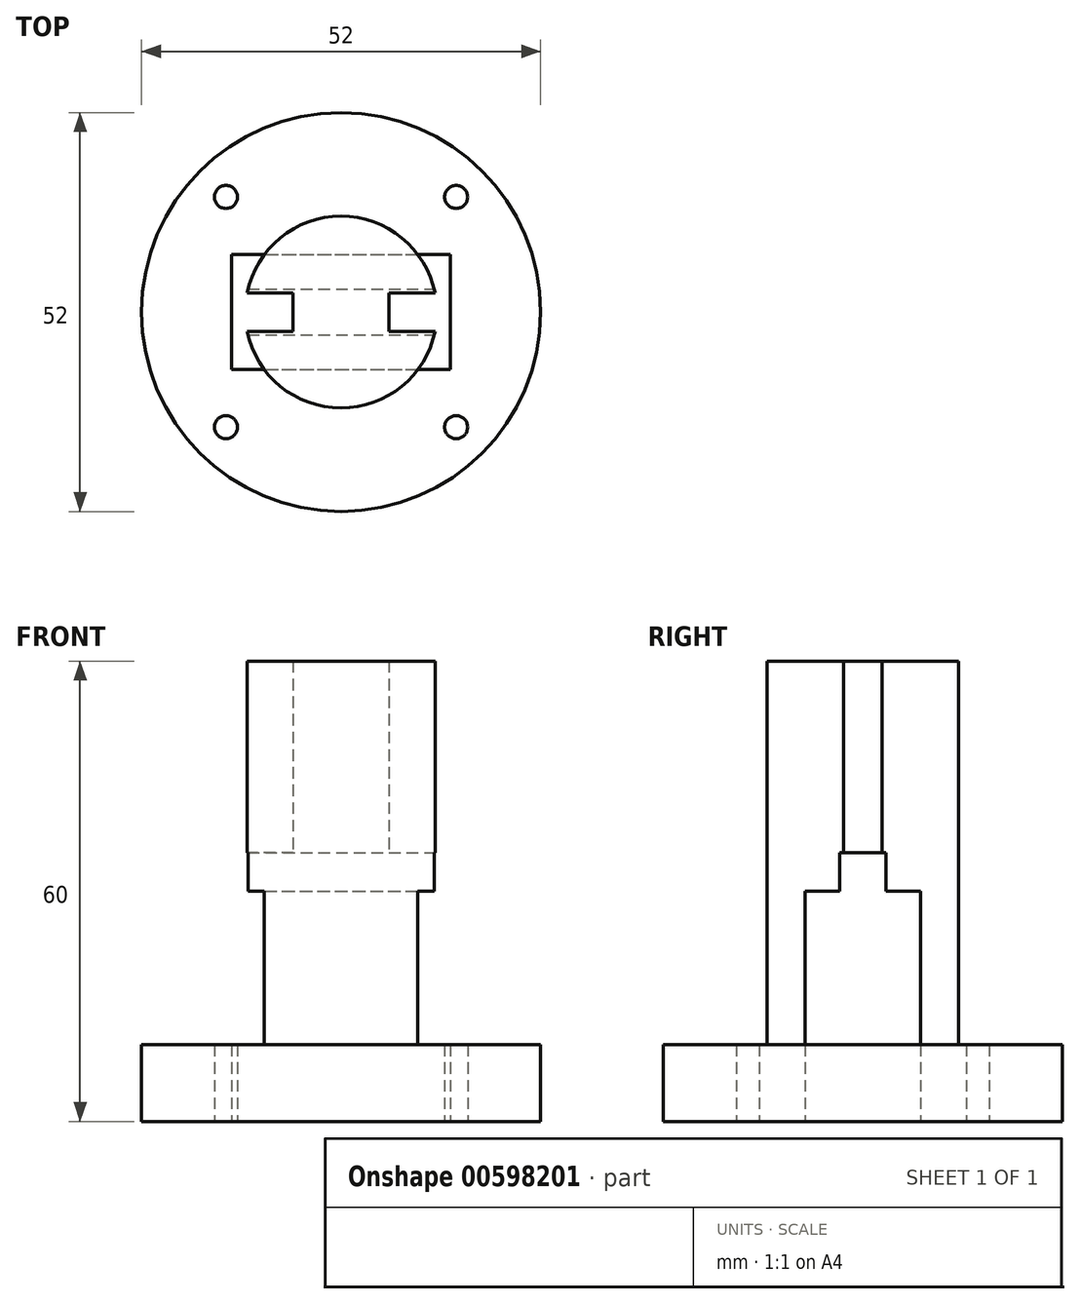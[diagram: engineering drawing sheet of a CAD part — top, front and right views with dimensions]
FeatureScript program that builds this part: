
annotation { "Feature Type Name" : "Feature", "Feature Type Description" : "" }
export const myFeature = defineFeature(function(context is Context, id is Id, definition is map)
    precondition{}
    {
        {
            var Q0;
            Q0=qCreatedBy(makeId("Front.planeOp"),FACE);
            var sketch = newSketch(context, id + "F0", { "sketchPlane" : qUnion([Q0])});
            skLineSegment(sketch, "E0.bottom", {"start": v(0, 23.95) * mm, "end": v(12.5, 23.95) * mm});
            skLineSegment(sketch, "E0.top", {"start": v(0, -26.05) * mm, "end": v(12.5, -26.05) * mm});
            skLineSegment(sketch, "E0.left", {"start": v(0, 23.95) * mm, "end": v(0, -26.05) * mm});
            skLineSegment(sketch, "E0.right", {"start": v(12.5, 23.95) * mm, "end": v(12.5, -26.05) * mm});
            skLineSegment(sketch, "E1.bottom", {"start": v(0, -26.05) * mm, "end": v(26, -26.05) * mm});
            skLineSegment(sketch, "E1.top", {"start": v(0, -36.05) * mm, "end": v(26, -36.05) * mm});
            skLineSegment(sketch, "E1.left", {"start": v(0, -26.05) * mm, "end": v(0, -36.05) * mm});
            skLineSegment(sketch, "E1.right", {"start": v(26, -26.05) * mm, "end": v(26, -36.05) * mm});
            skSolve(sketch);
        }
        {
            var Q0;
            Q0=makeQuery(id+"F0.imprint","IMPRINT",FACE,{"disambiguationData":[TD([[makeQuery(id+"F0.imprint","IMPRINT",EDGE,{"derivedFrom":sQuery(id+"F0.wireOp",EDGE,"E0.bottom")}),-1.0]])]});
            var Q1;
            Q1=makeQuery(id+"F0.imprint","IMPRINT",FACE,{"disambiguationData":[TD([[makeQuery(id+"F0.imprint","IMPRINT",EDGE,{"derivedFrom":sQuery(id+"F0.wireOp",EDGE,"E1.top")}),1.0]])]});
            var Q2;
            Q2=sQuery(id+"F0.wireOp",EDGE,"E0.left");
            revolve(context, id + "F1", {"entities" : qUnion([Q0, Q1]), "axis" : qUnion([Q2]), "revolveType" : RevolveType.FULL});
        }
        {
            var Q0;
            Q0=qCreatedBy(makeId("Top.planeOp"),FACE);
            var sketch = newSketch(context, id + "F2", { "sketchPlane" : qUnion([Q0])});
            skLineSegment(sketch, "E2.bottom", {"start": v(-14.25, 2.5) * mm, "end": v(-6.25, 2.5) * mm});
            skLineSegment(sketch, "E2.top", {"start": v(-14.25, -2.5) * mm, "end": v(-6.25, -2.5) * mm});
            skLineSegment(sketch, "E2.left", {"start": v(-14.25, 2.5) * mm, "end": v(-14.25, -2.5) * mm});
            skLineSegment(sketch, "E2.right", {"start": v(-6.25, 2.5) * mm, "end": v(-6.25, -2.5) * mm});
            skPoint(sketch, "E2.middle", {"position": v(-10.25, 0) * mm});
            skLineSegment(sketch, "E3.MirrorCS", {"start": v(6.25, 2.5) * mm, "end": v(6.25, -2.5) * mm});
            skLineSegment(sketch, "E4.MirrorCS", {"start": v(14.25, 2.5) * mm, "end": v(6.25, 2.5) * mm});
            skLineSegment(sketch, "E5.MirrorCS", {"start": v(14.25, 2.5) * mm, "end": v(14.25, -2.5) * mm});
            skLineSegment(sketch, "E6.MirrorCS", {"start": v(14.25, -2.5) * mm, "end": v(6.25, -2.5) * mm});
            skPoint(sketch, "E7.MirrorP", {"position": v(10.25, 0) * mm});
            skSolve(sketch);
        }
        {
            var Q0;
            Q0 = qSketchRegion(id + "F2", true);
            extrude(context, id + "F3", {"entities" : qUnion([Q0]), "operationType" : NewBodyOperationType.REMOVE, "endBound" : BoundingType.SYMMETRIC, "depth" : 75 * mm, "offsetDistance" : 25.4 * mm});
        }
        {
            var Q0;
            Q0=makeQuery(id+"F1.opRevolve","SWEPT_FACE",FACE,{"disambiguationData":[OSD([sQuery(id+"F0.wireOp",EDGE,"E1.top")])]});
            var sketch = newSketch(context, id + "F4", { "sketchPlane" : qUnion([Q0])});
            skLineSegment(sketch, "E8.bottom", {"start": v(-14.25, 3) * mm, "end": v(14.25, 3) * mm});
            skLineSegment(sketch, "E8.top", {"start": v(-14.25, -3) * mm, "end": v(14.25, -3) * mm});
            skLineSegment(sketch, "E8.left", {"start": v(-14.25, 3) * mm, "end": v(-14.25, -3) * mm});
            skLineSegment(sketch, "E8.right", {"start": v(14.25, 3) * mm, "end": v(14.25, -3) * mm});
            skPoint(sketch, "E8.middle", {"position": v(0, 0) * mm});
            skSolve(sketch);
        }
        {
            var Q0;
            Q0 = qSketchRegion(id + "F4", true);
            extrude(context, id + "F5", {"entities" : qUnion([Q0]), "operationType" : NewBodyOperationType.REMOVE, "oppositeDirection" : true, "depth" : 35 * mm, "offsetDistance" : 25.4 * mm});
        }
        {
            var Q0;
            Q0=makeQuery(id+"F1.opRevolve","SWEPT_FACE",FACE,{"disambiguationData":[OSD([sQuery(id+"F0.wireOp",EDGE,"E1.top")])]});
            var sketch = newSketch(context, id + "F6", { "sketchPlane" : qUnion([Q0])});
            skLineSegment(sketch, "E9.bottom", {"start": v(-14.25, -7.5) * mm, "end": v(14.25, -7.5) * mm});
            skLineSegment(sketch, "E9.top", {"start": v(-14.25, 7.5) * mm, "end": v(14.25, 7.5) * mm});
            skLineSegment(sketch, "E9.left", {"start": v(-14.25, -7.5) * mm, "end": v(-14.25, 7.5) * mm});
            skLineSegment(sketch, "E9.right", {"start": v(14.25, -7.5) * mm, "end": v(14.25, 7.5) * mm});
            skPoint(sketch, "E9.middle", {"position": v(0, 0) * mm});
            skCircle(sketch, "E10", {"center": v(15, -15) * mm, "radius": 1.5 * mm});
            skCircle(sketch, "E11.MirrorC", {"center": v(-15, -15) * mm, "radius": 1.5 * mm});
            skCircle(sketch, "E12.MirrorC", {"center": v(15, 15) * mm, "radius": 1.5 * mm});
            skCircle(sketch, "E13.MirrorC", {"center": v(-15, 15) * mm, "radius": 1.5 * mm});
            skSolve(sketch);
        }
        {
            var Q0;
            {var subQ0=sQuery(id+"F6.wireOp",EDGE,"E9.top");Q0=makeQuery(id+"F6.imprint","IMPRINT",FACE,{"disambiguationData":[TD([[makeQuery(id+"F6.imprint","IMPRINT",EDGE,{"derivedFrom":subQ0}),-1.0]])]});}
            var Q1;
            {var subQ0=sQuery(id+"F6.wireOp",EDGE,"E9.bottom");Q1=makeQuery(id+"F6.imprint","IMPRINT",FACE,{"disambiguationData":[TD([[makeQuery(id+"F6.imprint","IMPRINT",EDGE,{"derivedFrom":subQ0}),1.0]])]});}
            extrude(context, id + "F7", {"entities" : qUnion([Q0, Q1]), "operationType" : NewBodyOperationType.REMOVE, "oppositeDirection" : true, "depth" : 30 * mm, "offsetDistance" : 25.4 * mm});
        }
        {
            var Q0;
            Q0 = qSketchRegion(id + "F6", true);
            extrude(context, id + "F8", {"entities" : qUnion([Q0]), "operationType" : NewBodyOperationType.REMOVE, "oppositeDirection" : true, "depth" : 11 * mm, "offsetDistance" : 25.4 * mm});
        }
    });
